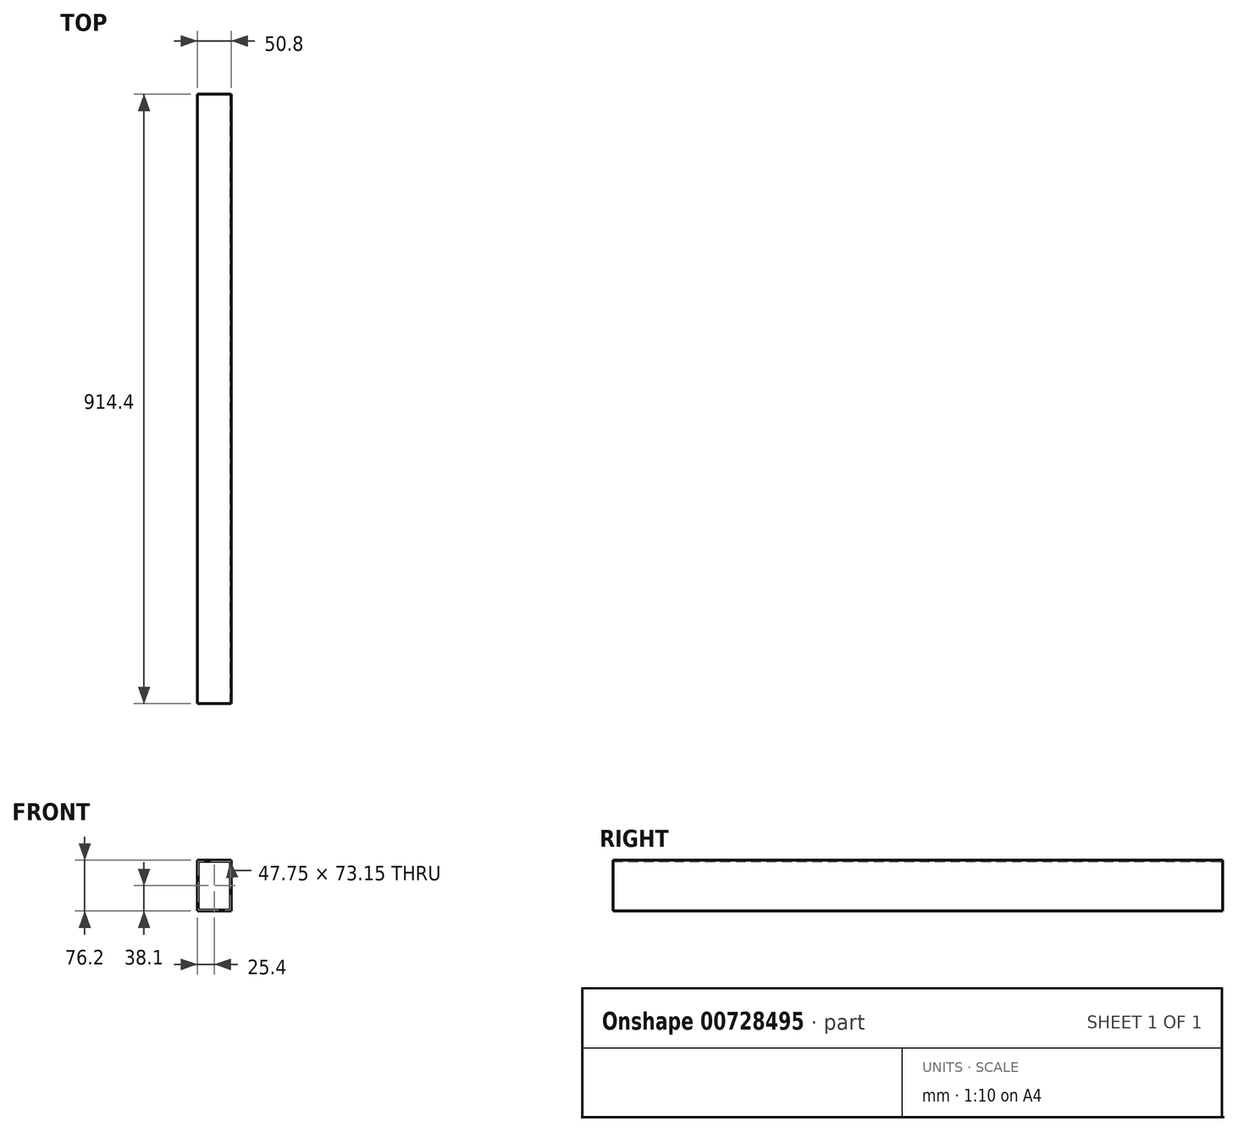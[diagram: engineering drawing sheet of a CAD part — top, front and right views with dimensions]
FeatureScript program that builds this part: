
annotation { "Feature Type Name" : "Feature", "Feature Type Description" : "" }
export const myFeature = defineFeature(function(context is Context, id is Id, definition is map)
    precondition{}
    {
        {
            var Q0;
            Q0=qCreatedBy(makeId("Front.planeOp"),FACE);
            var sketch = newSketch(context, id + "F0", { "sketchPlane" : qUnion([Q0])});
            skLineSegment(sketch, "E0.bottom", {"start": v(-25.4, 38.1) * mm, "end": v(25.4, 38.1) * mm});
            skLineSegment(sketch, "E0.top", {"start": v(-25.4, -38.1) * mm, "end": v(25.4, -38.1) * mm});
            skLineSegment(sketch, "E0.left", {"start": v(-25.4, 38.1) * mm, "end": v(-25.4, -38.1) * mm});
            skLineSegment(sketch, "E0.right", {"start": v(25.4, 38.1) * mm, "end": v(25.4, -38.1) * mm});
            skPoint(sketch, "E0.middle", {"position": v(0, 0) * mm});
            skLineSegment(sketch, "E1.bottom", {"start": v(-23.88, 36.58) * mm, "end": v(23.88, 36.58) * mm});
            skLineSegment(sketch, "E1.top", {"start": v(-23.88, -36.58) * mm, "end": v(23.88, -36.58) * mm});
            skLineSegment(sketch, "E1.left", {"start": v(-23.88, 36.58) * mm, "end": v(-23.88, -36.58) * mm});
            skLineSegment(sketch, "E1.right", {"start": v(23.88, 36.58) * mm, "end": v(23.88, -36.58) * mm});
            skSolve(sketch);
        }
        {
            var Q0;
            Q0=makeQuery(id+"F0.imprint","IMPRINT",FACE,{"disambiguationData":[TD([[makeQuery(id+"F0.imprint","IMPRINT",EDGE,{"derivedFrom":sQuery(id+"F0.wireOp",EDGE,"E0.bottom")}),-1.0]])]});
            extrude(context, id + "F1", {"entities" : qUnion([Q0]), "endBound" : BoundingType.SYMMETRIC, "depth" : 914.4 * mm, "offsetDistance" : 25.4 * mm});
        }
    });
